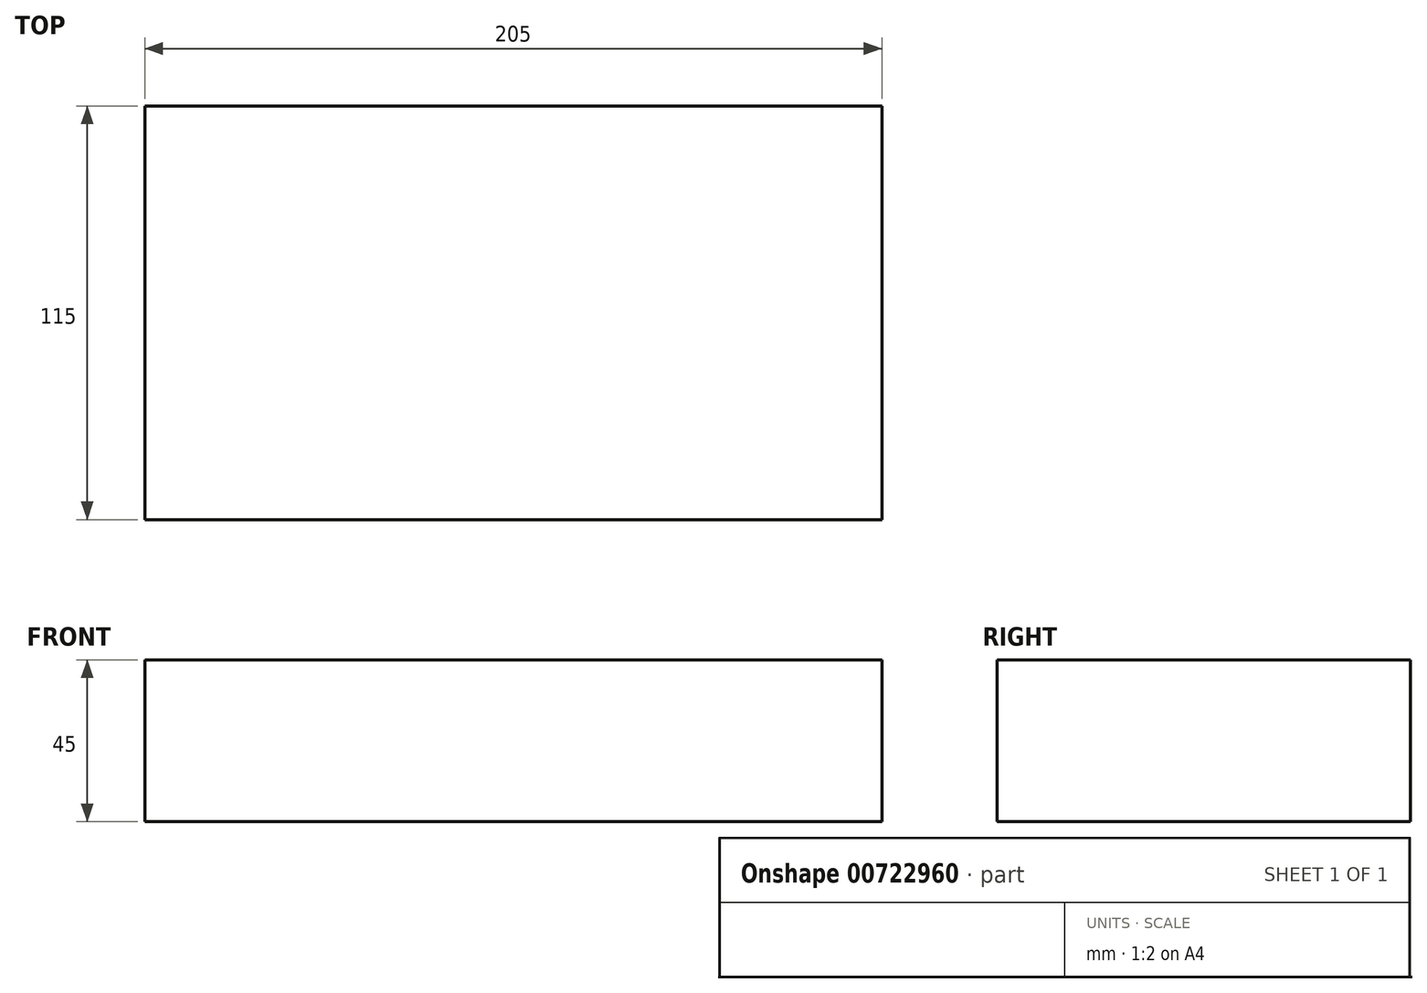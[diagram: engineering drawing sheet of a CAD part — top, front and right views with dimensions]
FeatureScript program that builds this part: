
annotation { "Feature Type Name" : "Feature", "Feature Type Description" : "" }
export const myFeature = defineFeature(function(context is Context, id is Id, definition is map)
    precondition{}
    {
        {
            var Q0;
            Q0=qCreatedBy(makeId("Top.planeOp"),FACE);
            var sketch = newSketch(context, id + "F0", { "sketchPlane" : qUnion([Q0])});
            skLineSegment(sketch, "E0.bottom", {"start": v(-102.5, 57.5) * mm, "end": v(102.5, 57.5) * mm});
            skLineSegment(sketch, "E0.top", {"start": v(-102.5, -57.5) * mm, "end": v(102.5, -57.5) * mm});
            skLineSegment(sketch, "E0.left", {"start": v(-102.5, 57.5) * mm, "end": v(-102.5, -57.5) * mm});
            skLineSegment(sketch, "E0.right", {"start": v(102.5, 57.5) * mm, "end": v(102.5, -57.5) * mm});
            skLineSegment(sketch, "E1", {"start": v(-102.5, 57.5) * mm, "end": v(102.5, -57.5) * mm, "construction": true});
            skLineSegment(sketch, "E2", {"start": v(102.5, 57.5) * mm, "end": v(-102.5, -57.5) * mm, "construction": true});
            skSolve(sketch);
        }
        {
            var Q0;
            Q0 = qSketchRegion(id + "F0", true);
            extrude(context, id + "F1", {"entities" : qUnion([Q0]), "depth" : 45 * mm, "offsetDistance" : 25 * mm});
        }
    });
